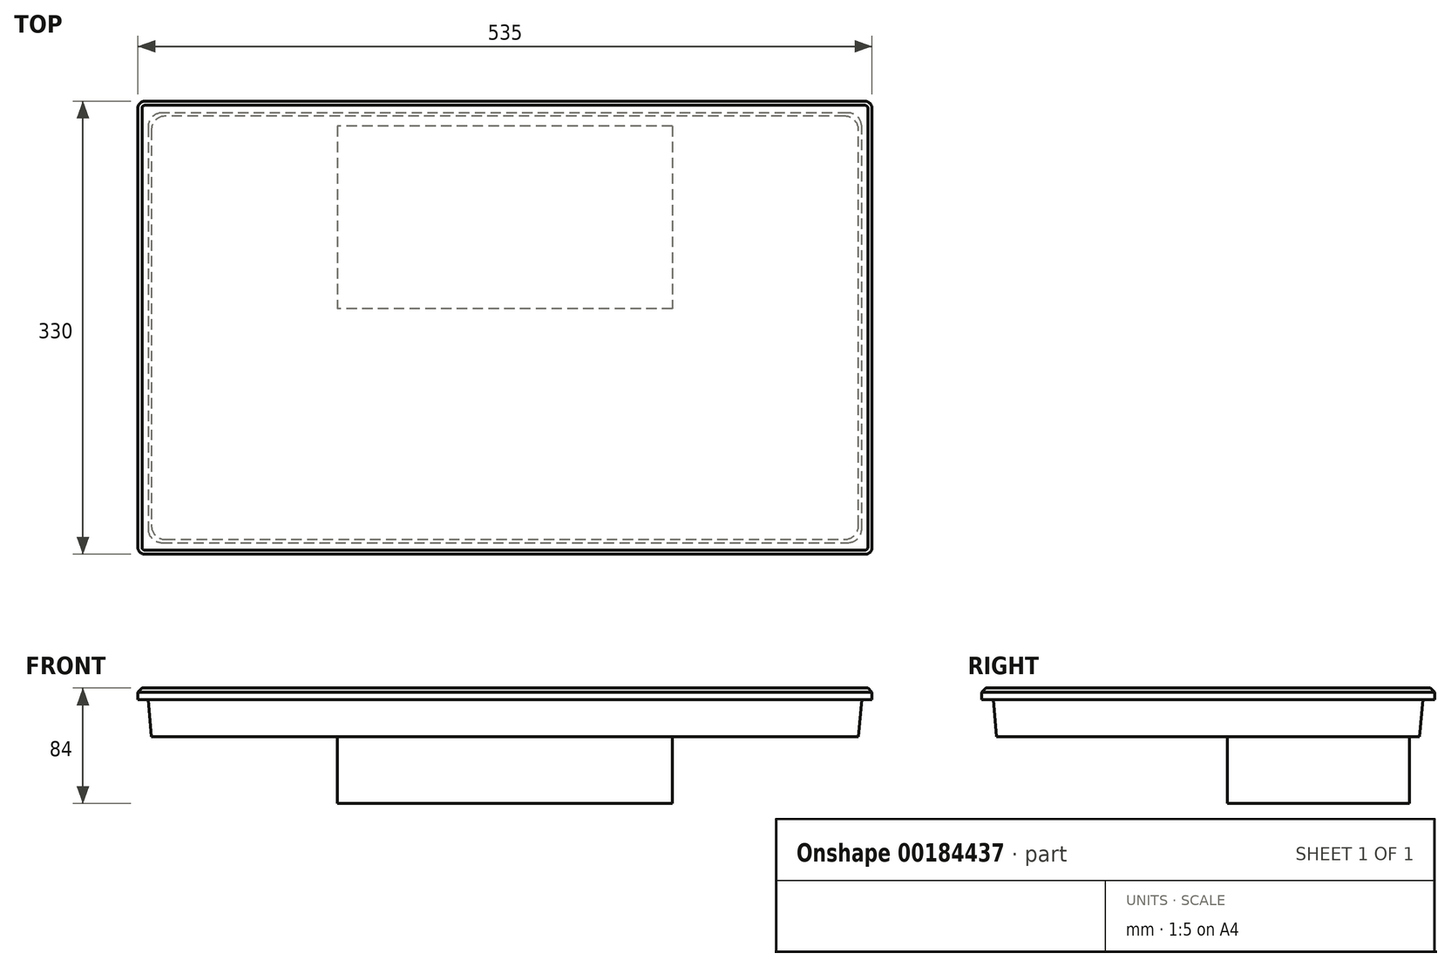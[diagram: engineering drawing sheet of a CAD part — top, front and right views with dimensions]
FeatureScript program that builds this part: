
annotation { "Feature Type Name" : "Feature", "Feature Type Description" : "" }
export const myFeature = defineFeature(function(context is Context, id is Id, definition is map)
    precondition{}
    {
        {
            var Q0;
            Q0=qCreatedBy(makeId("Top.planeOp"),FACE);
            var sketch = newSketch(context, id + "F0", { "sketchPlane" : qUnion([Q0])});
            skLineSegment(sketch, "E0.bottom", {"start": v(-267.5, 165) * mm, "end": v(267.5, 165) * mm});
            skLineSegment(sketch, "E0.top", {"start": v(-267.5, -165) * mm, "end": v(267.5, -165) * mm});
            skLineSegment(sketch, "E0.left", {"start": v(-267.5, 165) * mm, "end": v(-267.5, -165) * mm});
            skLineSegment(sketch, "E0.right", {"start": v(267.5, 165) * mm, "end": v(267.5, -165) * mm});
            skPoint(sketch, "E0.middle", {"position": v(0, 0) * mm});
            skLineSegment(sketch, "E1.bottom", {"start": v(260, 156.5) * mm, "end": v(-260, 156.5) * mm});
            skLineSegment(sketch, "E1.top", {"start": v(260, -156.5) * mm, "end": v(-260, -156.5) * mm});
            skLineSegment(sketch, "E1.left", {"start": v(260, 156.5) * mm, "end": v(260, -156.5) * mm});
            skLineSegment(sketch, "E1.right", {"start": v(-260, 156.5) * mm, "end": v(-260, -156.5) * mm});
            skSolve(sketch);
        }
        {
            var Q0;
            Q0=makeQuery(id+"F0.imprint","IMPRINT",FACE,{"disambiguationData":[TD([[makeQuery(id+"F0.imprint","IMPRINT",EDGE,{"derivedFrom":sQuery(id+"F0.wireOp",EDGE,"E0.bottom")}),-1.0]])]});
            var Q1;
            Q1=makeQuery(id+"F0.imprint","IMPRINT",FACE,{"disambiguationData":[TD([[makeQuery(id+"F0.imprint","IMPRINT",EDGE,{"derivedFrom":sQuery(id+"F0.wireOp",EDGE,"E1.bottom")}),1.0]])]});
            extrude(context, id + "F1", {"entities" : qUnion([Q0, Q1]), "depth" : 8.5 * mm});
        }
        {
            var Q0;
            Q0=makeQuery(id+"F0.imprint","IMPRINT",FACE,{"disambiguationData":[TD([[makeQuery(id+"F0.imprint","IMPRINT",EDGE,{"derivedFrom":sQuery(id+"F0.wireOp",EDGE,"E1.bottom")}),1.0]])]});
            extrude(context, id + "F2", {"entities" : qUnion([Q0]), "operationType" : NewBodyOperationType.ADD, "oppositeDirection" : true, "depth" : 27 * mm, "hasDraft" : true, "draftAngle" : 5 * degree, "draftPullDirection" : true});
        }
        {
            var Q0;
            Q0=makeQuery(id+"F2.opExtrude","CAP_FACE",FACE,{"disambiguationData":[OSD([sQuery(id+"F0.wireOp",EDGE,"E1.bottom"),sQuery(id+"F0.wireOp",EDGE,"E1.top"),sQuery(id+"F0.wireOp",EDGE,"E1.left"),sQuery(id+"F0.wireOp",EDGE,"E1.right")])],"isStart":false});
            var sketch = newSketch(context, id + "F3", { "sketchPlane" : qUnion([Q0])});
            skLineSegment(sketch, "E2.bottom", {"start": v(122, -146.86) * mm, "end": v(-122, -146.86) * mm});
            skLineSegment(sketch, "E2.top", {"start": v(122, -13.86) * mm, "end": v(-122, -13.86) * mm});
            skLineSegment(sketch, "E2.left", {"start": v(122, -146.86) * mm, "end": v(122, -13.86) * mm});
            skLineSegment(sketch, "E2.right", {"start": v(-122, -146.86) * mm, "end": v(-122, -13.86) * mm});
            skPoint(sketch, "E3", {"position": v(0, -13.86) * mm});
            skSolve(sketch);
        }
        {
            var Q0;
            Q0=makeQuery(id+"F3.imprint","IMPRINT",FACE,{"disambiguationData":[TD([[makeQuery(id+"F3.imprint","IMPRINT",EDGE,{"derivedFrom":sQuery(id+"F3.wireOp",EDGE,"E2.bottom")}),-1.0]])]});
            extrude(context, id + "F4", {"entities" : qUnion([Q0]), "operationType" : NewBodyOperationType.ADD, "depth" : 48.5 * mm});
        }
        {
            var Q0;
            Q0=makeQuery(id+"F1.opExtrude","SWEPT_EDGE",EDGE,{"disambiguationData":[OSD([sQuery(id+"F0.wireOp",EDGE,"E0.bottom"),sQuery(id+"F0.wireOp",EDGE,"E0.right")])]});
            var Q1;
            Q1=makeQuery(id+"F1.opExtrude","SWEPT_EDGE",EDGE,{"disambiguationData":[OSD([sQuery(id+"F0.wireOp",EDGE,"E0.bottom"),sQuery(id+"F0.wireOp",EDGE,"E0.left")])]});
            var Q2;
            Q2=makeQuery(id+"F1.opExtrude","SWEPT_EDGE",EDGE,{"disambiguationData":[OSD([sQuery(id+"F0.wireOp",EDGE,"E0.top"),sQuery(id+"F0.wireOp",EDGE,"E0.left")])]});
            var Q3;
            Q3=makeQuery(id+"F1.opExtrude","SWEPT_EDGE",EDGE,{"disambiguationData":[OSD([sQuery(id+"F0.wireOp",EDGE,"E0.top"),sQuery(id+"F0.wireOp",EDGE,"E0.right")])]});
            fillet(context, id + "F5", {"entities" : qUnion([Q0, Q1, Q2, Q3]), "radius" : 5 * mm, "allowEdgeOverflow" : false});
        }
        {
            var Q0;
            Q0=makeQuery(id+"F2.opExtrude","SWEPT_EDGE",EDGE,{"disambiguationData":[OSD([sQuery(id+"F0.wireOp",EDGE,"E1.top"),sQuery(id+"F0.wireOp",EDGE,"E1.left")])]});
            var Q1;
            Q1=makeQuery(id+"F2.opExtrude","SWEPT_EDGE",EDGE,{"disambiguationData":[OSD([sQuery(id+"F0.wireOp",EDGE,"E1.bottom"),sQuery(id+"F0.wireOp",EDGE,"E1.left")])]});
            var Q2;
            Q2=makeQuery(id+"F2.opExtrude","SWEPT_EDGE",EDGE,{"disambiguationData":[OSD([sQuery(id+"F0.wireOp",EDGE,"E1.bottom"),sQuery(id+"F0.wireOp",EDGE,"E1.right")])]});
            var Q3;
            Q3=makeQuery(id+"F2.opExtrude","SWEPT_EDGE",EDGE,{"disambiguationData":[OSD([sQuery(id+"F0.wireOp",EDGE,"E1.top"),sQuery(id+"F0.wireOp",EDGE,"E1.right")])]});
            fillet(context, id + "F6", {"entities" : qUnion([Q0, Q1, Q2, Q3]), "radius" : 10 * mm, "allowEdgeOverflow" : false});
        }
        {
            var Q0;
            Q0=makeQuery(id+"F1.opExtrude","CAP_EDGE",EDGE,{"disambiguationData":[OSD([sQuery(id+"F0.wireOp",EDGE,"E0.top")])],"isStart":false});
            chamfer(context, id + "F7", {"entities" : qUnion([Q0]), "width" : 3 * mm, "tangentPropagation" : true});
        }
    });
